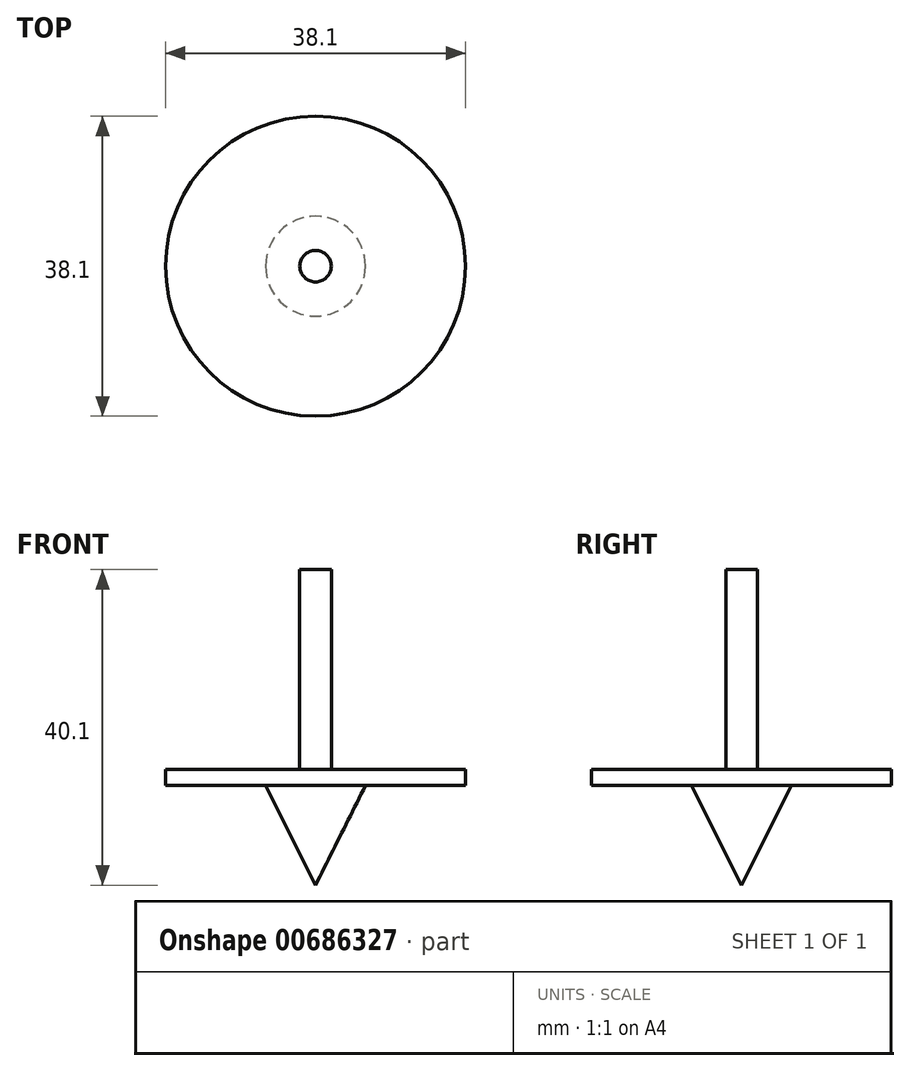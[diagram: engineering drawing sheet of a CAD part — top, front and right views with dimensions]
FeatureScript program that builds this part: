
annotation { "Feature Type Name" : "Feature", "Feature Type Description" : "" }
export const myFeature = defineFeature(function(context is Context, id is Id, definition is map)
    precondition{}
    {
        {
            var Q0;
            Q0=qCreatedBy(makeId("Front.planeOp"),FACE);
            var sketch = newSketch(context, id + "F0", { "sketchPlane" : qUnion([Q0])});
            skLineSegment(sketch, "E0", {"start": v(0, 0) * mm, "end": v(-19.05, 0) * mm});
            skLineSegment(sketch, "E1", {"start": v(-19.05, 0) * mm, "end": v(-19.05, 2) * mm});
            skLineSegment(sketch, "E2", {"start": v(-19.05, 2) * mm, "end": v(0, 2) * mm});
            skLineSegment(sketch, "E3", {"start": v(0, 2) * mm, "end": v(0, 0) * mm});
            skLineSegment(sketch, "E4", {"start": v(0, 2) * mm, "end": v(0, 27.4) * mm});
            skLineSegment(sketch, "E5", {"start": v(0, 27.4) * mm, "end": v(-2, 27.4) * mm});
            skLineSegment(sketch, "E6", {"start": v(-2, 27.4) * mm, "end": v(-2, 2) * mm});
            skLineSegment(sketch, "E7", {"start": v(0, 0) * mm, "end": v(0, -12.7) * mm});
            skLineSegment(sketch, "E8", {"start": v(0, -12.7) * mm, "end": v(-6.34, 0) * mm});
            skSolve(sketch);
        }
        {
            var Q0;
            Q0 = qSketchRegion(id + "F0", true);
            var Q1;
            Q1=sQuery(id+"F0.wireOp",EDGE,"E4");
            revolve(context, id + "F1", {"entities" : qUnion([Q0]), "axis" : qUnion([Q1]), "revolveType" : RevolveType.FULL});
        }
    });
